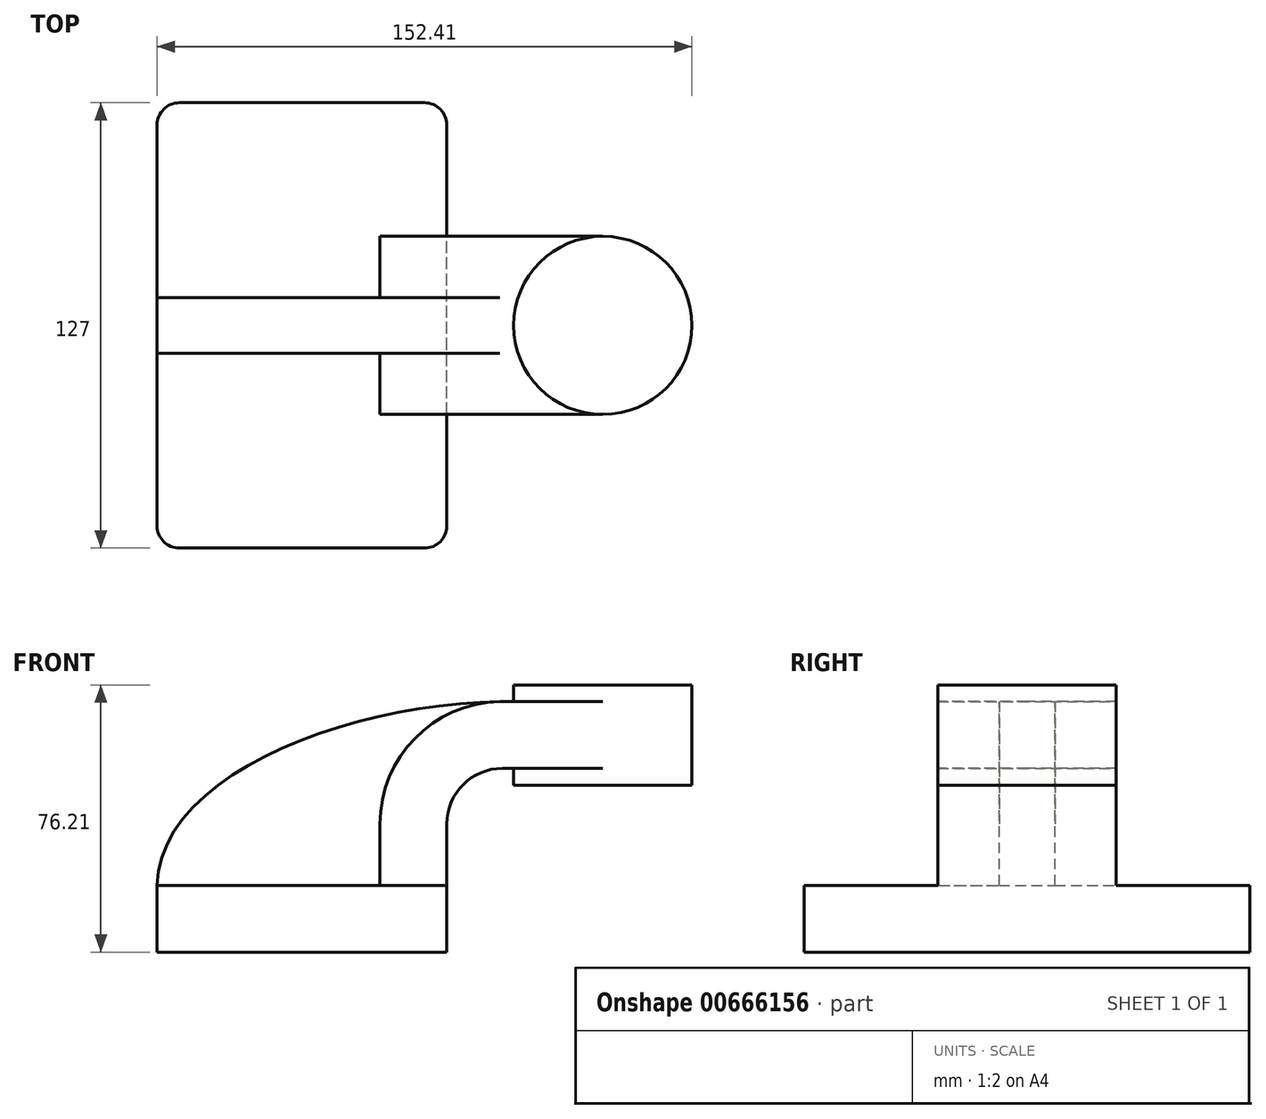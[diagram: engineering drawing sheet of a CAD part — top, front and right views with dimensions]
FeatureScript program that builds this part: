
annotation { "Feature Type Name" : "Feature", "Feature Type Description" : "" }
export const myFeature = defineFeature(function(context is Context, id is Id, definition is map)
    precondition{}
    {
        {
            var Q0;
            Q0=qCreatedBy(makeId("Front.planeOp"),FACE);
            var sketch = newSketch(context, id + "F0", { "sketchPlane" : qUnion([Q0])});
            skLineSegment(sketch, "E0.bottom", {"start": v(-41.28, 9.53) * mm, "end": v(41.28, 9.52) * mm});
            skLineSegment(sketch, "E0.top", {"start": v(-41.28, -9.52) * mm, "end": v(41.28, -9.53) * mm});
            skLineSegment(sketch, "E0.left", {"start": v(-41.28, 9.52) * mm, "end": v(-41.28, -9.52) * mm});
            skLineSegment(sketch, "E0.right", {"start": v(41.28, 9.52) * mm, "end": v(41.28, -9.52) * mm});
            skLineSegment(sketch, "E1", {"start": v(41.28, 9.52) * mm, "end": v(41.28, 27) * mm});
            skArc(sketch, "E2", {"start": v(41.28, 27) * mm, "mid": v(45.92, 38.23) * mm, "end": v(57.15, 42.88) * mm});
            skLineSegment(sketch, "E3", {"start": v(57.15, 42.88) * mm, "end": v(85.72, 42.88) * mm});
            skLineSegment(sketch, "E4.bottom", {"start": v(111.12, 38.1) * mm, "end": v(60.33, 38.1) * mm});
            skLineSegment(sketch, "E4.top", {"start": v(111.12, 66.67) * mm, "end": v(60.33, 66.67) * mm});
            skLineSegment(sketch, "E4.left", {"start": v(111.13, 38.1) * mm, "end": v(111.13, 66.67) * mm});
            skLineSegment(sketch, "E4.right", {"start": v(60.33, 38.1) * mm, "end": v(60.33, 66.67) * mm});
            skPoint(sketch, "E4.middle", {"position": v(85.72, 52.39) * mm});
            skLineSegment(sketch, "E5.0", {"start": v(57.15, 61.93) * mm, "end": v(85.72, 61.93) * mm});
            skArc(sketch, "E5.1", {"start": v(22.23, 27) * mm, "mid": v(32.45, 51.7) * mm, "end": v(57.15, 61.93) * mm});
            skLineSegment(sketch, "E5.2", {"start": v(22.23, 9.53) * mm, "end": v(22.23, 27) * mm});
            skFitSpline(sketch, "E6", {"points": [v(-41.27, 9.52) * mm, v(57.15, 61.93) * mm], "startDerivative": vector(1.7, 95.75) * mm, "endDerivative": vector(128.2, 1.1) * mm});
            skLineSegment(sketch, "E7", {"start": v(85.72, 38.1) * mm, "end": v(85.72, 66.68) * mm});
            skSolve(sketch);
        }
        {
            var Q0;
            Q0=makeQuery(id+"F0.imprint","IMPRINT",FACE,{"disambiguationData":[TD([[makeQuery(id+"F0.imprint","IMPRINT",EDGE,{"derivedFrom":sQuery(id+"F0.wireOp",EDGE,"E0.top")}),1.0]])]});
            extrude(context, id + "F1", {"entities" : qUnion([Q0]), "endBound" : BoundingType.SYMMETRIC, "depth" : 127 * mm, "offsetDistance" : 25.4 * mm});
        }
        {
            var Q0;
            {var subQ4=sQuery(id+"F0.wireOp",EDGE,"E1");Q0=makeQuery(id+"F0.imprint","IMPRINT",FACE,{"disambiguationData":[TD([[makeQuery(id+"F0.imprint","IMPRINT",EDGE,{"derivedFrom":subQ4}),1.0]])]});}
            var Q1;
            {var subQ0=sQuery(id+"F0.wireOp",EDGE,"E7");var subQ1=sQuery(id+"F0.wireOp",EDGE,"E3");var subQ2=makeQuery(id+"F0.imprint","INTERSECT",VERTEX,{"derivedFrom":[subQ1,subQ0]});Q1=makeQuery(id+"F0.imprint","IMPRINT",FACE,{"disambiguationData":[TD([[makeQuery(id+"F0.imprint","IMPRINT",EDGE,{"disambiguationData":[TD([[subQ2,1.0]])],"derivedFrom":subQ1}),1.0]])]});}
            extrude(context, id + "F2", {"entities" : qUnion([Q0, Q1]), "operationType" : NewBodyOperationType.ADD, "endBound" : BoundingType.SYMMETRIC, "depth" : 50.8 * mm, "offsetDistance" : 25.4 * mm});
        }
        {
            var Q0;
            {var subQ3=sQuery(id+"F0.wireOp",EDGE,"E5.2");Q0=makeQuery(id+"F0.imprint","IMPRINT",FACE,{"disambiguationData":[TD([[makeQuery(id+"F0.imprint","IMPRINT",EDGE,{"derivedFrom":subQ3}),1.0]])]});}
            extrude(context, id + "F3", {"entities" : qUnion([Q0]), "operationType" : NewBodyOperationType.ADD, "endBound" : BoundingType.SYMMETRIC, "depth" : 15.88 * mm, "offsetDistance" : 25.4 * mm});
        }
        {
            var Q0;
            {var subQ0=sQuery(id+"F0.wireOp",EDGE,"E4.left");Q0=makeQuery(id+"F0.imprint","IMPRINT",FACE,{"disambiguationData":[TD([[makeQuery(id+"F0.imprint","IMPRINT",EDGE,{"derivedFrom":subQ0}),1.0]])]});}
            var Q1;
            Q1=sQuery(id+"F0.wireOp",EDGE,"E7");
            revolve(context, id + "F4", {"operationType" : NewBodyOperationType.ADD, "entities" : qUnion([Q0]), "axis" : qUnion([Q1]), "revolveType" : RevolveType.FULL});
        }
        {
            var Q0;
            Q0=makeQuery(id+"F1.opExtrude","CAP_EDGE",EDGE,{"disambiguationData":[OSD([sQuery(id+"F0.wireOp",EDGE,"E0.right")])],"isStart":false});
            var Q1;
            Q1=makeQuery(id+"F1.opExtrude","CAP_EDGE",EDGE,{"disambiguationData":[OSD([sQuery(id+"F0.wireOp",EDGE,"E0.left")])],"isStart":false});
            var Q2;
            Q2=makeQuery(id+"F1.opExtrude","CAP_EDGE",EDGE,{"disambiguationData":[OSD([sQuery(id+"F0.wireOp",EDGE,"E0.right")])],"isStart":true});
            var Q3;
            Q3=makeQuery(id+"F1.opExtrude","CAP_EDGE",EDGE,{"disambiguationData":[OSD([sQuery(id+"F0.wireOp",EDGE,"E0.left")])],"isStart":true});
            fillet(context, id + "F5", {"entities" : qUnion([Q0, Q1, Q2, Q3]), "radius" : 6.35 * mm, "tangentPropagation" : true, "allowEdgeOverflow" : false});
        }
    });
